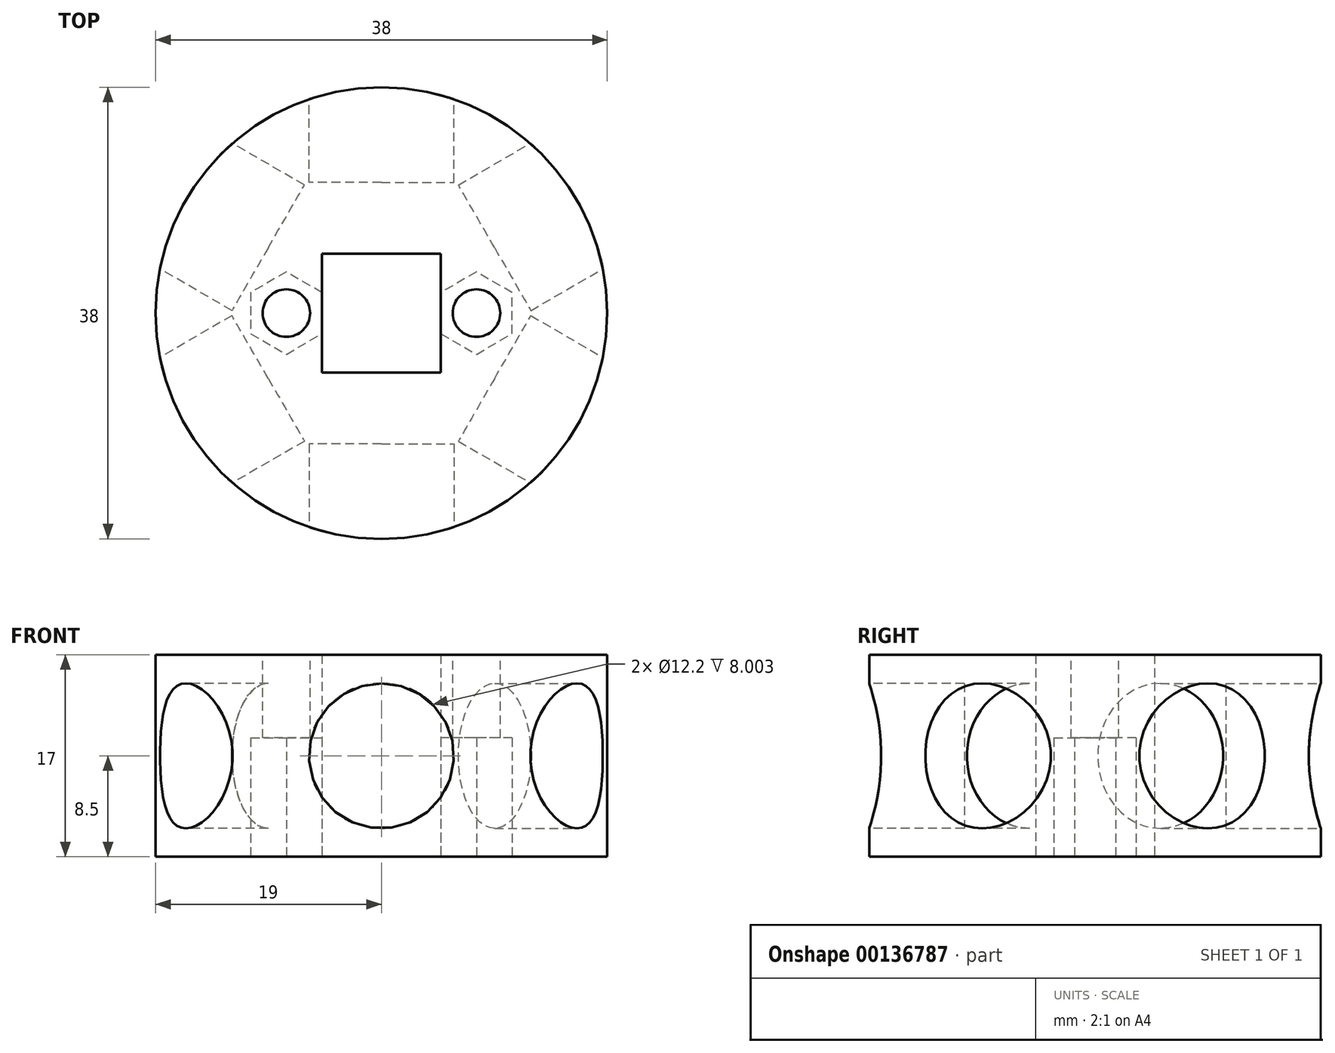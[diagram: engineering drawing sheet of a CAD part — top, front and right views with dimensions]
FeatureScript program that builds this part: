
annotation { "Feature Type Name" : "Feature", "Feature Type Description" : "" }
export const myFeature = defineFeature(function(context is Context, id is Id, definition is map)
    precondition{}
    {
        {
            var Q0;
            Q0=qCreatedBy(makeId("Top.planeOp"),FACE);
            var sketch = newSketch(context, id + "F0", { "sketchPlane" : qUnion([Q0])});
            skCircle(sketch, "E0", {"center": v(0, 0) * mm, "radius": 19 * mm});
            skPoint(sketch, "E1", {"position": v(-9.5, 16.45) * mm});
            skPoint(sketch, "E2.1.0", {"position": v(-19, 0) * mm});
            skPoint(sketch, "E2.2.0", {"position": v(-9.5, -16.45) * mm});
            skPoint(sketch, "E2.3.0", {"position": v(9.5, -16.45) * mm});
            skPoint(sketch, "E2.4.0", {"position": v(19, 0) * mm});
            skPoint(sketch, "E2.5.0", {"position": v(9.5, 16.45) * mm});
            skLineSegment(sketch, "E2.anchor1", {"start": v(0, 0) * mm, "end": v(-9.5, 16.45) * mm, "construction": true});
            skLineSegment(sketch, "E2.anchor2", {"start": v(0, 0) * mm, "end": v(9.5, 16.45) * mm, "construction": true});
            skLineSegment(sketch, "E3", {"start": v(-9.5, 16.45) * mm, "end": v(9.5, -16.45) * mm});
            skLineSegment(sketch, "E4", {"start": v(9.5, 16.45) * mm, "end": v(-9.5, -16.45) * mm});
            skPoint(sketch, "E5", {"position": v(0, 19) * mm});
            skSolve(sketch);
        }
        {
            var Q0;
            {var subQ0=sQuery(id+"F0.wireOp",EDGE,"E3");var subQ1=sQuery(id+"F0.wireOp",EDGE,"E0");var subQ2=makeQuery(id+"F0.imprint","INTERSECT",VERTEX,{"disambiguationData":[OD(0.0)],"derivedFrom":[subQ1,subQ0]});Q0=makeQuery(id+"F0.imprint","IMPRINT",FACE,{"disambiguationData":[TD([[makeQuery(id+"F0.imprint","IMPRINT",EDGE,{"disambiguationData":[TD([[subQ2,1.0]])],"derivedFrom":subQ1}),1.0]])]});}
            extrude(context, id + "F1", {"entities" : qUnion([Q0]), "depth" : 17 * mm});
        }
        {
            var Q0;
            Q0=qCreatedBy(makeId("Front.planeOp"),FACE);
            cPlane(context, id + "F2", {"entities" : qUnion([Q0]), "cplaneType" : CPlaneType.OFFSET, "offset" : 20 * mm, "oppositeDirection" : true, "width" : 150 * mm, "height" : 150 * mm});
        }
        {
            var Q0;
            Q0=qCreatedBy(makeId("Top.planeOp"),FACE);
            cPlane(context, id + "F3", {"entities" : qUnion([Q0]), "cplaneType" : CPlaneType.OFFSET, "offset" : 8.5 * mm, "width" : 150 * mm, "height" : 150 * mm});
        }
        {
            var Q0;
            Q0=qCreatedBy(id+"F3.planeOp",FACE);
            var sketch = newSketch(context, id + "F4", { "sketchPlane" : qUnion([Q0])});
            skPoint(sketch, "E6", {"position": v(0, 19) * mm});
            skSolve(sketch);
        }
        {
            var Q0;
            Q0=qCreatedBy(id+"F2.planeOp",FACE);
            var sketch = newSketch(context, id + "F5", { "sketchPlane" : qUnion([Q0])});
            skCircle(sketch, "E7", {"center": v(0, 8.5) * mm, "radius": 6.1 * mm});
            skSolve(sketch);
        }
        {
            var Q0;
            Q0=makeQuery(id+"F5.imprint","IMPRINT",FACE,{"disambiguationData":[TD([[makeQuery(id+"F5.imprint","IMPRINT",EDGE,{"derivedFrom":sQuery(id+"F5.wireOp",EDGE,"E7")}),1.0]])]});
            extrude(context, id + "F6", {"entities" : qUnion([Q0]), "operationType" : NewBodyOperationType.REMOVE, "depth" : 9 * mm});
        }
        {
            var Q0;
            Q0=makeQuery(id+"F1.opExtrude","SWEPT_BODY",BODY,{"disambiguationData":[OSD([sQuery(id+"F0.wireOp",EDGE,"E0"),sQuery(id+"F0.wireOp",EDGE,"E3"),sQuery(id+"F0.wireOp",EDGE,"E4")])]});
            var Q1;
            Q1=sQuery(id+"F0.wireOp",EDGE,"E0");
            circularPattern(context, id + "F7", {"operationType" : NewBodyOperationType.ADD, "entities" : qUnion([Q0]), "axis" : qUnion([Q1]), "angle" : 360 * degree, "instanceCount" : 6, "equalSpace" : true});
        }
        {
            var Q0;
            {var subQ0=makeQuery(id+"F1.opExtrude","CAP_FACE",FACE,{"disambiguationData":[OSD([sQuery(id+"F0.wireOp",EDGE,"E0"),sQuery(id+"F0.wireOp",EDGE,"E3"),sQuery(id+"F0.wireOp",EDGE,"E4")])],"isStart":true});Q0=makeQuery(id+"F7.boolean.opBoolean","MERGE",FACE,{"derivedFrom":[subQ0,makeQuery(id+"F7.opPattern","COPY",FACE,{"derivedFrom":subQ0,"instanceName":"1"}),makeQuery(id+"F7.opPattern","COPY",FACE,{"derivedFrom":subQ0,"instanceName":"2"}),makeQuery(id+"F7.opPattern","COPY",FACE,{"derivedFrom":subQ0,"instanceName":"3"}),makeQuery(id+"F7.opPattern","COPY",FACE,{"derivedFrom":subQ0,"instanceName":"4"}),makeQuery(id+"F7.opPattern","COPY",FACE,{"derivedFrom":subQ0,"instanceName":"5"})]});}
            var sketch = newSketch(context, id + "F8", { "sketchPlane" : qUnion([Q0])});
            skLineSegment(sketch, "E8", {"start": v(0, 19) * mm, "end": v(0, 0) * mm});
            skLineSegment(sketch, "E9", {"start": v(0, 0) * mm, "end": v(9.5, 16.45) * mm});
            skPoint(sketch, "E10", {"position": v(8, 13.86) * mm});
            skPoint(sketch, "E11.center", {"position": v(0, 0) * mm});
            skPoint(sketch, "E12.1.0", {"position": v(-13.86, 8) * mm});
            skPoint(sketch, "E12.2.0", {"position": v(-8, -13.86) * mm});
            skPoint(sketch, "E12.3.0", {"position": v(13.86, -8) * mm});
            skLineSegment(sketch, "E13.bottom", {"start": v(5, -5) * mm, "end": v(-5, -5) * mm});
            skLineSegment(sketch, "E13.top", {"start": v(5, 5) * mm, "end": v(-5, 5) * mm});
            skLineSegment(sketch, "E13.left", {"start": v(5, -5) * mm, "end": v(5, 5) * mm});
            skLineSegment(sketch, "E13.right", {"start": v(-5, -5) * mm, "end": v(-5, 5) * mm});
            skPoint(sketch, "E14", {"position": v(-8, 0) * mm});
            skPoint(sketch, "E14.positionSnap0", {"position": v(-5, 0) * mm});
            skPoint(sketch, "E15", {"position": v(8, 0) * mm});
            skPoint(sketch, "E15.positionSnap0", {"position": v(5, 0) * mm});
            skCircle(sketch, "E16", {"center": v(0, 0) * mm, "radius": 2.1 * mm});
            skLineSegment(sketch, "E17", {"start": v(-1.1, 1.79) * mm, "end": v(-1.1, -1.79) * mm});
            skLineSegment(sketch, "E18", {"start": v(1.1, 1.79) * mm, "end": v(1.1, -1.79) * mm});
            skSolve(sketch);
        }
        {
            var Q0;
            Q0=sQuery(id+"F8.wireOp",VERTEX,"E14");
            var Q1;
            Q1=sQuery(id+"F8.wireOp",VERTEX,"E15");
            var Q2;
            Q2=makeQuery(id+"F1.opExtrude","SWEPT_BODY",BODY,{"disambiguationData":[OSD([sQuery(id+"F0.wireOp",EDGE,"E0"),sQuery(id+"F0.wireOp",EDGE,"E3"),sQuery(id+"F0.wireOp",EDGE,"E4")])]});
            hole(context, id + "F9", {"style" : HoleStyle.SIMPLE, "endStyle" : HoleEndStyle.THROUGH, "holeDiameter" : 4 * mm, "tappedDepth" : 12 * mm, "tapClearance" : 3, "locations" : qUnion([Q0, Q1]), "scope" : qUnion([Q2])});
        }
        {
            var Q0;
            {var subQ0=makeQuery(id+"F1.opExtrude","CAP_FACE",FACE,{"disambiguationData":[OSD([sQuery(id+"F0.wireOp",EDGE,"E0"),sQuery(id+"F0.wireOp",EDGE,"E3"),sQuery(id+"F0.wireOp",EDGE,"E4")])],"isStart":true});Q0=makeQuery(id+"F7.boolean.opBoolean","MERGE",FACE,{"derivedFrom":[subQ0,makeQuery(id+"F7.opPattern","COPY",FACE,{"derivedFrom":subQ0,"instanceName":"1"}),makeQuery(id+"F7.opPattern","COPY",FACE,{"derivedFrom":subQ0,"instanceName":"2"}),makeQuery(id+"F7.opPattern","COPY",FACE,{"derivedFrom":subQ0,"instanceName":"3"}),makeQuery(id+"F7.opPattern","COPY",FACE,{"derivedFrom":subQ0,"instanceName":"4"}),makeQuery(id+"F7.opPattern","COPY",FACE,{"derivedFrom":subQ0,"instanceName":"5"})]});}
            var sketch = newSketch(context, id + "F10", { "sketchPlane" : qUnion([Q0])});
            skPoint(sketch, "E19", {"position": v(-23.77, -16.37) * mm});
            skPoint(sketch, "E20.2.0", {"position": v(16.07, 6.63) * mm});
            skPoint(sketch, "E20.center", {"position": v(16.07, -39.37) * mm});
            skLineSegment(sketch, "E20.anchor1", {"start": v(16.07, -39.37) * mm, "end": v(-23.77, -16.37) * mm, "construction": true});
            skLineSegment(sketch, "E20.anchor2", {"start": v(16.07, -39.37) * mm, "end": v(16.07, 6.63) * mm, "construction": true});
            skCircle(sketch, "E21.cCircle", {"center": v(-8, 0) * mm, "radius": 3 * mm, "construction": true});
            skLineSegment(sketch, "E21.0", {"start": v(-5, 1.73) * mm, "end": v(-5, -1.73) * mm});
            skLineSegment(sketch, "E21.1", {"start": v(-5, -1.73) * mm, "end": v(-8, -3.46) * mm});
            skLineSegment(sketch, "E21.2", {"start": v(-8, -3.46) * mm, "end": v(-11, -1.73) * mm});
            skLineSegment(sketch, "E21.3", {"start": v(-11, -1.73) * mm, "end": v(-11, 1.73) * mm});
            skLineSegment(sketch, "E21.4", {"start": v(-11, 1.73) * mm, "end": v(-8, 3.46) * mm});
            skLineSegment(sketch, "E21.5", {"start": v(-8, 3.46) * mm, "end": v(-5, 1.73) * mm});
            skPoint(sketch, "E21.0.midPoint", {"position": v(-5, 0) * mm});
            skPoint(sketch, "E22", {"position": v(-8.84, -16.84) * mm});
            skPoint(sketch, "E23.1.0", {"position": v(8, 0) * mm});
            skPoint(sketch, "E23.2.0", {"position": v(31, 6.16) * mm});
            skPoint(sketch, "E23.center", {"position": v(31, -39.84) * mm});
            skLineSegment(sketch, "E23.anchor1", {"start": v(31, -39.84) * mm, "end": v(-8.84, -16.84) * mm, "construction": true});
            skLineSegment(sketch, "E23.anchor2", {"start": v(31, -39.84) * mm, "end": v(31, 6.16) * mm, "construction": true});
            skCircle(sketch, "E24.cCircle", {"center": v(8, 0) * mm, "radius": 3 * mm, "construction": true});
            skLineSegment(sketch, "E24.0", {"start": v(5, -1.73) * mm, "end": v(5, 1.73) * mm});
            skLineSegment(sketch, "E24.1", {"start": v(5, 1.73) * mm, "end": v(8, 3.46) * mm});
            skLineSegment(sketch, "E24.2", {"start": v(8, 3.46) * mm, "end": v(11, 1.73) * mm});
            skLineSegment(sketch, "E24.3", {"start": v(11, 1.73) * mm, "end": v(11, -1.73) * mm});
            skLineSegment(sketch, "E24.4", {"start": v(11, -1.73) * mm, "end": v(8, -3.46) * mm});
            skLineSegment(sketch, "E24.5", {"start": v(8, -3.46) * mm, "end": v(5, -1.73) * mm});
            skPoint(sketch, "E24.0.midPoint", {"position": v(5, 0) * mm});
            skSolve(sketch);
        }
        {
            var Q0;
            Q0=makeQuery(id+"F10.imprint","IMPRINT",FACE,{"disambiguationData":[TD([[makeQuery(id+"F10.imprint","IMPRINT",EDGE,{"derivedFrom":sQuery(id+"F10.wireOp",EDGE,"E21.0")}),-1.0]])]});
            var Q1;
            Q1=makeQuery(id+"F10.imprint","IMPRINT",FACE,{"disambiguationData":[TD([[makeQuery(id+"F10.imprint","IMPRINT",EDGE,{"derivedFrom":sQuery(id+"F10.wireOp",EDGE,"E24.0")}),-1.0]])]});
            extrude(context, id + "F11", {"entities" : qUnion([Q0, Q1]), "operationType" : NewBodyOperationType.REMOVE, "oppositeDirection" : true, "depth" : 10 * mm});
        }
        {
            var Q0;
            Q0=makeQuery(id+"F8.imprint","IMPRINT",FACE,{"disambiguationData":[TD([[makeQuery(id+"F8.imprint","IMPRINT",EDGE,{"derivedFrom":sQuery(id+"F8.wireOp",EDGE,"E13.bottom")}),-1.0]])]});
            var Q1;
            {var subQ0=sQuery(id+"F8.wireOp",EDGE,"E13.top");var subQ1=sQuery(id+"F8.wireOp",EDGE,"E8");var subQ2=makeQuery(id+"F8.imprint","INTERSECT",VERTEX,{"derivedFrom":[subQ1,subQ0]});Q1=makeQuery(id+"F8.imprint","IMPRINT",FACE,{"disambiguationData":[TD([[makeQuery(id+"F8.imprint","IMPRINT",EDGE,{"disambiguationData":[TD([[subQ2,-1.0]])],"derivedFrom":subQ1}),1.0]])]});}
            var Q2;
            {var subQ0=sQuery(id+"F8.wireOp",EDGE,"E17");Q2=makeQuery(id+"F8.imprint","IMPRINT",FACE,{"disambiguationData":[TD([[makeQuery(id+"F8.imprint","IMPRINT",EDGE,{"derivedFrom":subQ0}),1.0]])]});}
            var Q3;
            {var subQ0=sQuery(id+"F8.wireOp",EDGE,"E17");Q3=makeQuery(id+"F8.imprint","IMPRINT",FACE,{"disambiguationData":[TD([[makeQuery(id+"F8.imprint","IMPRINT",EDGE,{"derivedFrom":subQ0}),-1.0]])]});}
            var Q4;
            {var subQ0=sQuery(id+"F8.wireOp",EDGE,"E18");Q4=makeQuery(id+"F8.imprint","IMPRINT",FACE,{"disambiguationData":[TD([[makeQuery(id+"F8.imprint","IMPRINT",EDGE,{"derivedFrom":subQ0}),1.0]])]});}
            var Q5;
            {var subQ0=sQuery(id+"F8.wireOp",EDGE,"E9");var subQ1=sQuery(id+"F8.wireOp",EDGE,"E8");var subQ2=makeQuery(id+"F8.imprint","INTERSECT",VERTEX,{"derivedFrom":[subQ1,subQ0]});Q5=makeQuery(id+"F8.imprint","IMPRINT",FACE,{"disambiguationData":[TD([[makeQuery(id+"F8.imprint","IMPRINT",EDGE,{"disambiguationData":[TD([[subQ2,1.0]])],"derivedFrom":subQ1}),1.0]])]});}
            extrude(context, id + "F12", {"entities" : qUnion([Q0, Q1, Q2, Q3, Q4, Q5]), "operationType" : NewBodyOperationType.REMOVE, "endBound" : BoundingType.THROUGH_ALL, "oppositeDirection" : true, "depth" : 10 * mm});
        }
    });
